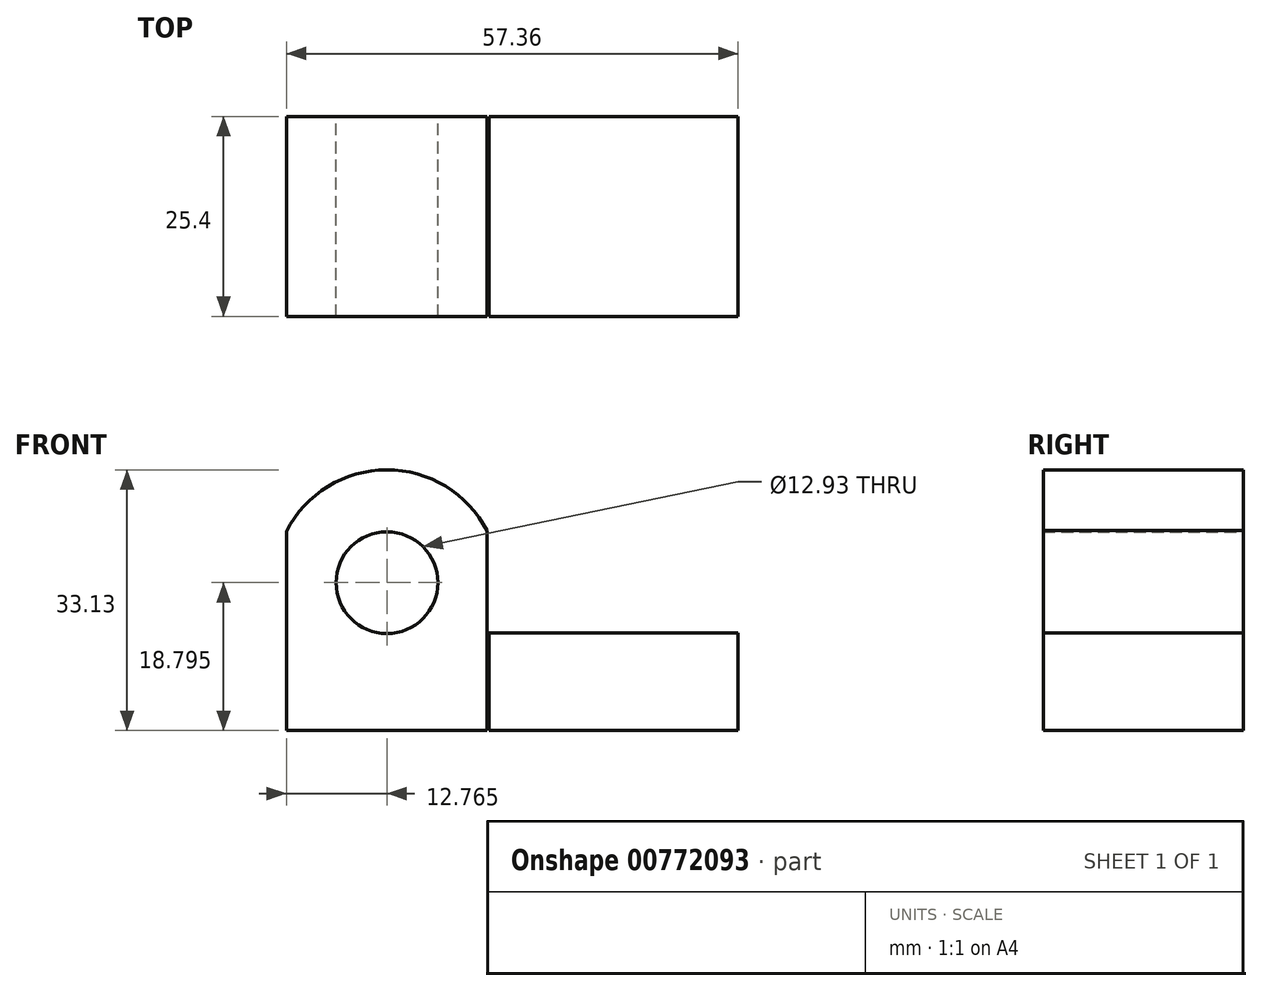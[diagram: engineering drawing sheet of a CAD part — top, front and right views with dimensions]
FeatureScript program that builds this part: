
annotation { "Feature Type Name" : "Feature", "Feature Type Description" : "" }
export const myFeature = defineFeature(function(context is Context, id is Id, definition is map)
    precondition{}
    {
        {
            var Q0;
            Q0=qCreatedBy(makeId("Front.planeOp"),FACE);
            var sketch = newSketch(context, id + "F0", { "sketchPlane" : qUnion([Q0])});
            skLineSegment(sketch, "E0", {"start": v(0, 0) * mm, "end": v(0, 25.31) * mm});
            skLineSegment(sketch, "E1", {"start": v(0, 0) * mm, "end": v(25.49, 0) * mm});
            skLineSegment(sketch, "E2", {"start": v(25.49, 12.7) * mm, "end": v(25.49, 25.4) * mm});
            skArc(sketch, "E3", {"start": v(25.49, 25.4) * mm, "mid": v(12.72, 33.13) * mm, "end": v(0, 25.31) * mm});
            skCircle(sketch, "E4", {"center": v(12.76, 18.8) * mm, "radius": 6.47 * mm});
            skLineSegment(sketch, "E5", {"start": v(25.49, 12.7) * mm, "end": v(25.49, 0) * mm});
            skSolve(sketch);
        }
        {
            var Q0;
            Q0=makeQuery(id+"F0.imprint","IMPRINT",FACE,{"disambiguationData":[TD([[makeQuery(id+"F0.imprint","IMPRINT",EDGE,{"derivedFrom":sQuery(id+"F0.wireOp",EDGE,"E0")}),-1.0]])]});
            extrude(context, id + "F1", {"entities" : qUnion([Q0]), "depth" : 25.4 * mm, "offsetDistance" : 25.4 * mm});
        }
        {
            var Q0;
            Q0=qCreatedBy(makeId("Front.planeOp"),FACE);
            var sketch = newSketch(context, id + "F2", { "sketchPlane" : qUnion([Q0])});
            skLineSegment(sketch, "E6", {"start": v(57.36, 0) * mm, "end": v(57.36, 12.4) * mm});
            skLineSegment(sketch, "E7", {"start": v(57.36, 12.4) * mm, "end": v(25.73, 12.4) * mm});
            skLineSegment(sketch, "E8", {"start": v(25.73, 12.4) * mm, "end": v(25.73, 0) * mm});
            skLineSegment(sketch, "E9", {"start": v(25.73, 0) * mm, "end": v(57.36, 0) * mm});
            skSolve(sketch);
        }
        {
            var Q0;
            Q0=makeQuery(id+"F2.imprint","IMPRINT",FACE,{"disambiguationData":[TD([[makeQuery(id+"F2.imprint","IMPRINT",EDGE,{"derivedFrom":sQuery(id+"F2.wireOp",EDGE,"E6")}),1.0]])]});
            extrude(context, id + "F3", {"entities" : qUnion([Q0]), "depth" : 25.4 * mm, "offsetDistance" : 25.4 * mm});
        }
    });
